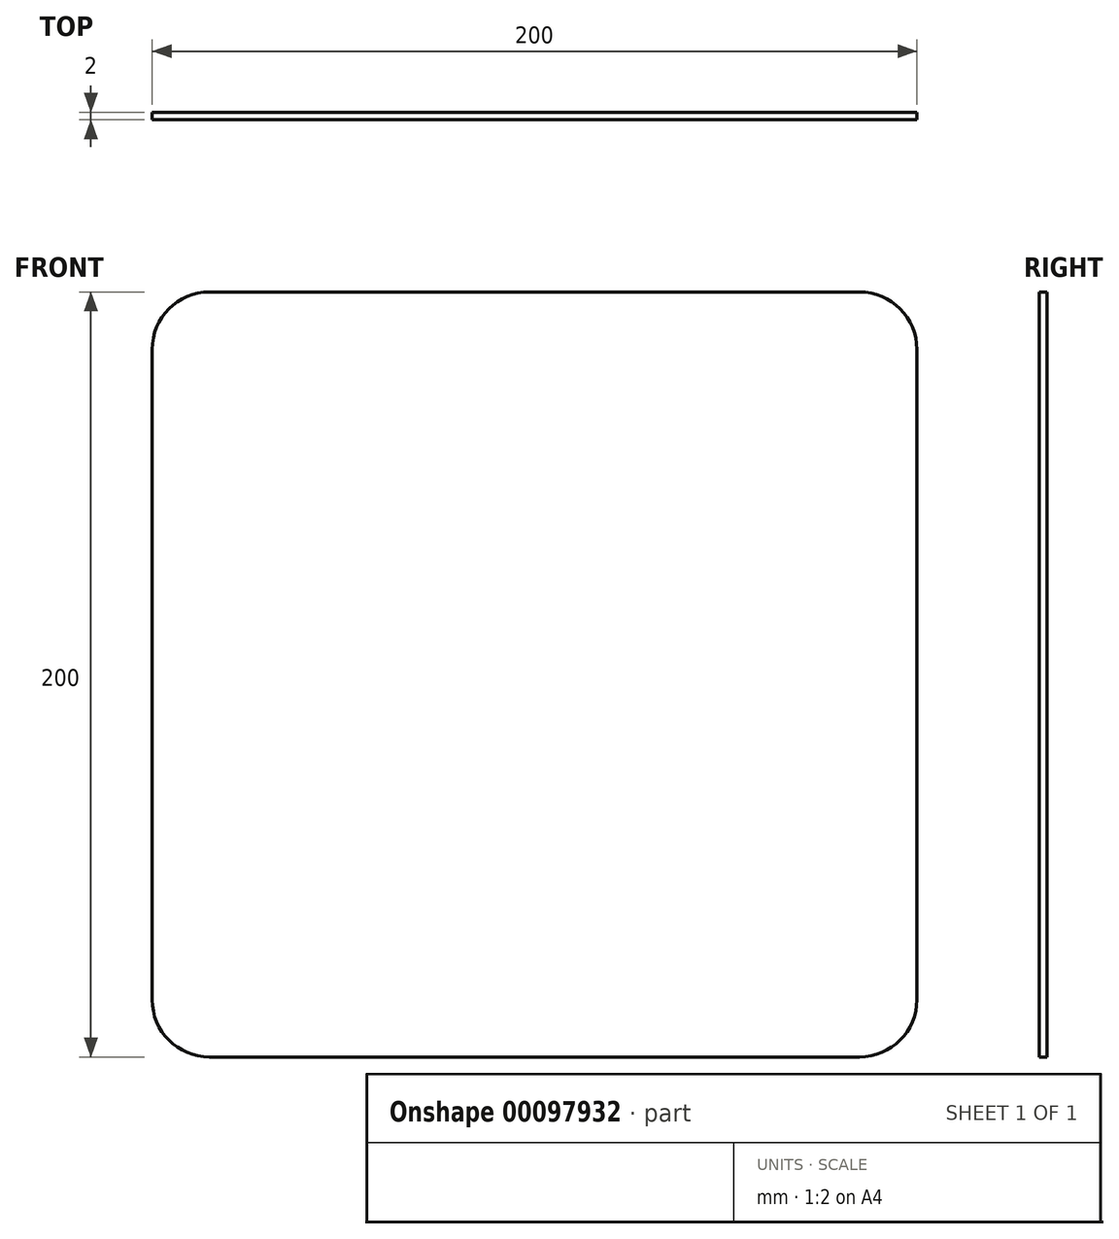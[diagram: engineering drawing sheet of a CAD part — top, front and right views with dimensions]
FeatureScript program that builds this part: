
annotation { "Feature Type Name" : "Feature", "Feature Type Description" : "" }
export const myFeature = defineFeature(function(context is Context, id is Id, definition is map)
    precondition{}
    {
        {
            var Q0;
            Q0=qCreatedBy(makeId("Front.planeOp"),FACE);
            var sketch = newSketch(context, id + "F0", { "sketchPlane" : qUnion([Q0])});
            skLineSegment(sketch, "E0.bottom", {"start": v(-100, 100) * mm, "end": v(100, 100) * mm});
            skLineSegment(sketch, "E0.top", {"start": v(-100, -100) * mm, "end": v(100, -100) * mm});
            skLineSegment(sketch, "E0.left", {"start": v(-100, 100) * mm, "end": v(-100, -100) * mm});
            skLineSegment(sketch, "E0.right", {"start": v(100, 100) * mm, "end": v(100, -100) * mm});
            skSolve(sketch);
        }
        {
            var Q0;
            Q0=makeQuery(id+"F0.imprint","IMPRINT",FACE,{"disambiguationData":[TD([[makeQuery(id+"F0.imprint","IMPRINT",EDGE,{"derivedFrom":sQuery(id+"F0.wireOp",EDGE,"E0.bottom")}),-1.0]])]});
            extrude(context, id + "F1", {"entities" : qUnion([Q0]), "endBound" : BoundingType.SYMMETRIC, "depth" : 2 * mm});
        }
        {
            var Q0;
            Q0=makeQuery(id+"F1.opExtrude","SWEPT_EDGE",EDGE,{"disambiguationData":[OSD([sQuery(id+"F0.wireOp",EDGE,"E0.bottom"),sQuery(id+"F0.wireOp",EDGE,"E0.right")])]});
            var Q1;
            Q1=makeQuery(id+"F1.opExtrude","SWEPT_EDGE",EDGE,{"disambiguationData":[OSD([sQuery(id+"F0.wireOp",EDGE,"E0.bottom"),sQuery(id+"F0.wireOp",EDGE,"E0.left")])]});
            var Q2;
            Q2=makeQuery(id+"F1.opExtrude","SWEPT_EDGE",EDGE,{"disambiguationData":[OSD([sQuery(id+"F0.wireOp",EDGE,"E0.top"),sQuery(id+"F0.wireOp",EDGE,"E0.left")])]});
            var Q3;
            Q3=makeQuery(id+"F1.opExtrude","SWEPT_EDGE",EDGE,{"disambiguationData":[OSD([sQuery(id+"F0.wireOp",EDGE,"E0.top"),sQuery(id+"F0.wireOp",EDGE,"E0.right")])]});
            fillet(context, id + "F2", {"entities" : qUnion([Q0, Q1, Q2, Q3]), "radius" : 15 * mm, "tangentPropagation" : true, "allowEdgeOverflow" : false});
        }
    });
